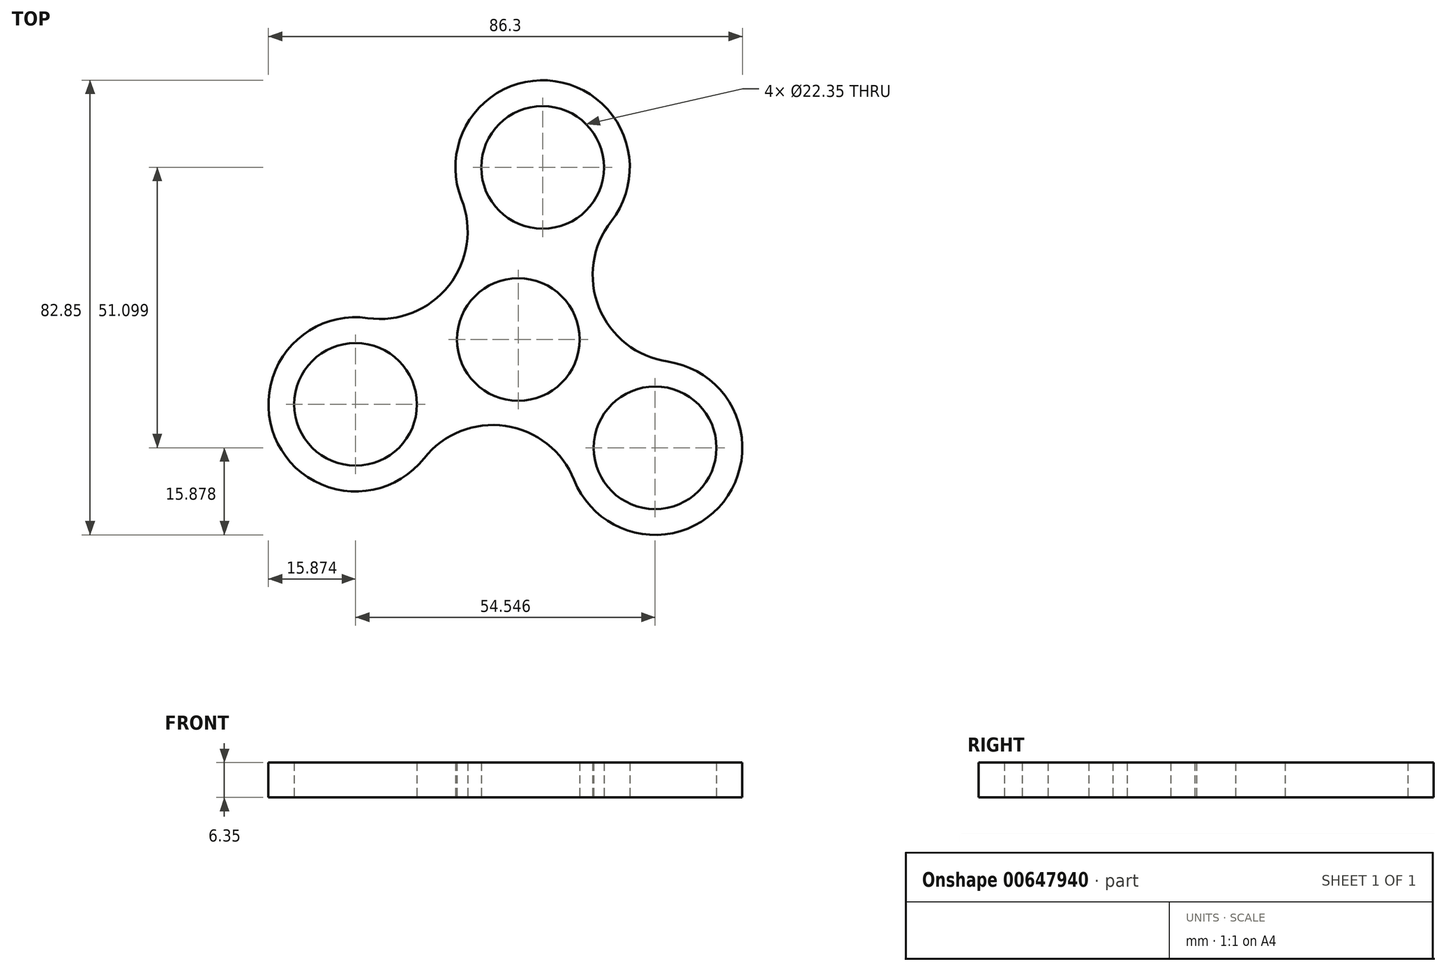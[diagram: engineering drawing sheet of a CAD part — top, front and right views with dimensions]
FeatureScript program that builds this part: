
annotation { "Feature Type Name" : "Feature", "Feature Type Description" : "" }
export const myFeature = defineFeature(function(context is Context, id is Id, definition is map)
    precondition{}
    {
        {
            var Q0;
            Q0=qCreatedBy(makeId("Top.planeOp"),FACE);
            var sketch = newSketch(context, id + "F0", { "sketchPlane" : qUnion([Q0])});
            skArc(sketch, "E0", {"start": v(-27.4, 3.9) * mm, "mid": v(-12.66, 9.82) * mm, "end": v(-10.34, 25.54) * mm});
            skArc(sketch, "E1", {"start": v(16.93, 21.59) * mm, "mid": v(6.7, 47.08) * mm, "end": v(-10.34, 25.54) * mm});
            skArc(sketch, "E2", {"start": v(-27.4, 3.9) * mm, "mid": v(-44.36, -17.72) * mm, "end": v(-17.16, -21.64) * mm});
            skArc(sketch, "E3", {"start": v(10.17, -25.61) * mm, "mid": v(-2.35, -15.74) * mm, "end": v(-17.16, -21.64) * mm});
            skArc(sketch, "E4", {"start": v(16.93, 21.59) * mm, "mid": v(14.7, 5.82) * mm, "end": v(27.2, -4.02) * mm});
            skArc(sketch, "E5", {"start": v(10.17, -25.61) * mm, "mid": v(37.39, -29.56) * mm, "end": v(27.2, -4.02) * mm});
            skCircle(sketch, "E6", {"center": v(0, 0) * mm, "radius": 11.18 * mm});
            skCircle(sketch, "E7", {"center": v(-29.63, -11.81) * mm, "radius": 11.18 * mm});
            skCircle(sketch, "E8", {"center": v(4.43, 31.37) * mm, "radius": 11.18 * mm});
            skCircle(sketch, "E9", {"center": v(24.92, -19.73) * mm, "radius": 11.18 * mm});
            skSolve(sketch);
        }
        {
            var Q0;
            Q0=makeQuery(id+"F0.imprint","IMPRINT",FACE,{"disambiguationData":[TD([[makeQuery(id+"F0.imprint","IMPRINT",EDGE,{"derivedFrom":sQuery(id+"F0.wireOp",EDGE,"E0")}),-1.0]])]});
            extrude(context, id + "F1", {"entities" : qUnion([Q0]), "depth" : 6.35 * mm, "offsetDistance" : 25.4 * mm});
        }
    });
